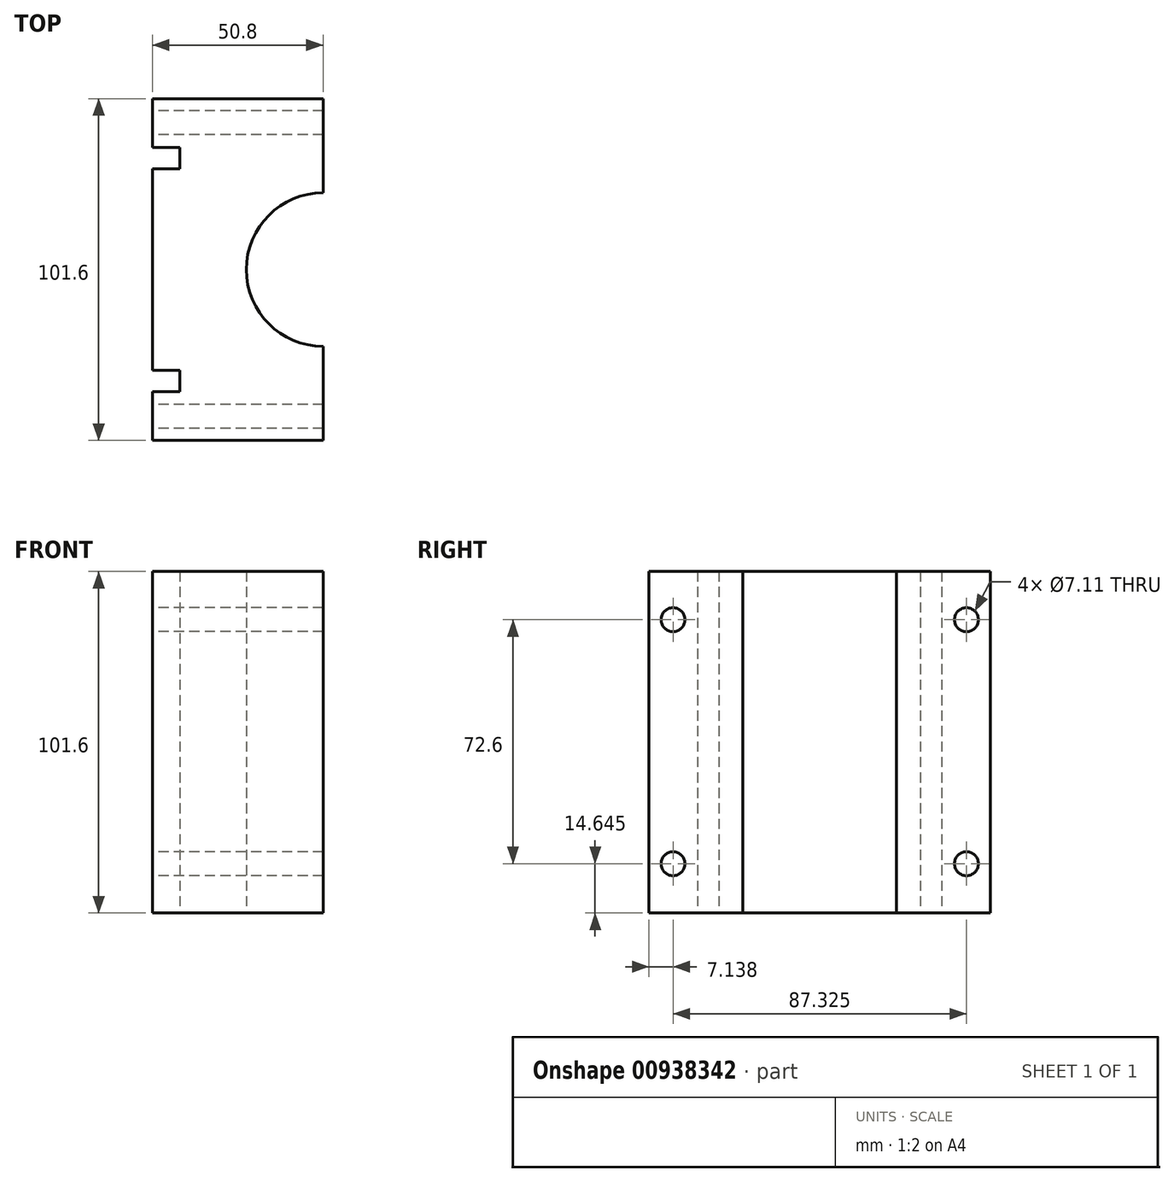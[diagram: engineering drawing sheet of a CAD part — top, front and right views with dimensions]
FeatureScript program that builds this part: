
annotation { "Feature Type Name" : "Feature", "Feature Type Description" : "" }
export const myFeature = defineFeature(function(context is Context, id is Id, definition is map)
    precondition{}
    {
        {
            var Q0;
            Q0=qCreatedBy(makeId("Top.planeOp"),FACE);
            var sketch = newSketch(context, id + "F0", { "sketchPlane" : qUnion([Q0])});
            skLineSegment(sketch, "E0.bottom", {"start": v(0, 0) * mm, "end": v(-50.8, 0) * mm});
            skLineSegment(sketch, "E0.top", {"start": v(0, 50.8) * mm, "end": v(-50.8, 50.8) * mm});
            skLineSegment(sketch, "E0.left", {"start": v(0, 0) * mm, "end": v(0, 50.8) * mm});
            skLineSegment(sketch, "E0.right", {"start": v(-50.8, 0) * mm, "end": v(-50.8, 50.8) * mm});
            skLineSegment(sketch, "E1.MirrorCS", {"start": v(0, 0) * mm, "end": v(0, -50.8) * mm});
            skLineSegment(sketch, "E2.MirrorCS", {"start": v(0, -50.8) * mm, "end": v(-50.8, -50.8) * mm});
            skLineSegment(sketch, "E3.MirrorCS", {"start": v(-50.8, 0) * mm, "end": v(-50.8, -50.8) * mm});
            skLineSegment(sketch, "E4", {"start": v(-50.8, 50.8) * mm, "end": v(-50.8, 36.32) * mm});
            skLineSegment(sketch, "E5", {"start": v(-50.8, 36.32) * mm, "end": v(-50.8, 29.97) * mm});
            skLineSegment(sketch, "E6", {"start": v(-50.8, 29.97) * mm, "end": v(-42.6, 29.97) * mm});
            skLineSegment(sketch, "E7", {"start": v(-42.6, 29.97) * mm, "end": v(-42.6, 36.32) * mm});
            skLineSegment(sketch, "E8", {"start": v(-42.6, 36.32) * mm, "end": v(-50.8, 36.32) * mm});
            skLineSegment(sketch, "E9.MirrorCS", {"start": v(-42.6, -36.32) * mm, "end": v(-50.8, -36.32) * mm});
            skLineSegment(sketch, "E10.MirrorCS", {"start": v(-50.8, -29.97) * mm, "end": v(-42.6, -29.97) * mm});
            skLineSegment(sketch, "E11.MirrorCS", {"start": v(-42.6, -29.97) * mm, "end": v(-42.6, -36.32) * mm});
            skCircle(sketch, "E12", {"center": v(0, 0) * mm, "radius": 22.86 * mm});
            skSolve(sketch);
        }
        {
            var Q0;
            {var subQ2=sQuery(id+"F0.wireOp",EDGE,"E0.top");Q0=makeQuery(id+"F0.imprint","IMPRINT",FACE,{"disambiguationData":[TD([[makeQuery(id+"F0.imprint","IMPRINT",EDGE,{"derivedFrom":subQ2}),1.0]])]});}
            var Q1;
            {var subQ4=sQuery(id+"F0.wireOp",EDGE,"E2.MirrorCS");Q1=makeQuery(id+"F0.imprint","IMPRINT",FACE,{"disambiguationData":[TD([[makeQuery(id+"F0.imprint","IMPRINT",EDGE,{"derivedFrom":subQ4}),-1.0]])]});}
            extrude(context, id + "F1", {"entities" : qUnion([Q0, Q1]), "depth" : 50.8 * mm, "offsetDistance" : 25.4 * mm});
        }
        {
            var Q0;
            Q0=makeQuery(id+"F1.opExtrude","CAP_FACE",FACE,{"disambiguationData":[OSD([sQuery(id+"F0.wireOp",EDGE,"E0.top"),sQuery(id+"F0.wireOp",EDGE,"E0.left"),sQuery(id+"F0.wireOp",EDGE,"E0.right"),sQuery(id+"F0.wireOp",EDGE,"E1.MirrorCS"),sQuery(id+"F0.wireOp",EDGE,"E2.MirrorCS"),sQuery(id+"F0.wireOp",EDGE,"E3.MirrorCS"),sQuery(id+"F0.wireOp",EDGE,"E4"),sQuery(id+"F0.wireOp",EDGE,"E6"),sQuery(id+"F0.wireOp",EDGE,"E7"),sQuery(id+"F0.wireOp",EDGE,"E8"),sQuery(id+"F0.wireOp",EDGE,"E9.MirrorCS"),sQuery(id+"F0.wireOp",EDGE,"E10.MirrorCS"),sQuery(id+"F0.wireOp",EDGE,"E11.MirrorCS"),sQuery(id+"F0.wireOp",EDGE,"E12")])],"isStart":false});
            extrude(context, id + "F2", {"entities" : qUnion([Q0]), "operationType" : NewBodyOperationType.ADD, "depth" : 50.8 * mm, "offsetDistance" : 25.4 * mm});
        }
        {
            var Q0;
            {var subQ0=sQuery(id+"F0.wireOp",EDGE,"E3.MirrorCS");Q0=makeQuery(id+"F2.boolean.opBoolean","MERGE",FACE,{"derivedFrom":[makeQuery(id+"F1.opExtrude","SWEPT_FACE",FACE,{"disambiguationData":[OSD([subQ0])]}),makeQuery(id+"F2.opExtrude","SWEPT_FACE",FACE,{"disambiguationData":[OSD([subQ0])]})]});}
            var sketch = newSketch(context, id + "F3", { "sketchPlane" : qUnion([Q0])});
            skCircle(sketch, "E13", {"center": v(43.66, 87.24) * mm, "radius": 5.08 * mm});
            skCircle(sketch, "E14.MirrorC", {"center": v(-43.66, 87.24) * mm, "radius": 5.08 * mm});
            skCircle(sketch, "E15", {"center": v(43.66, 14.65) * mm, "radius": 5.08 * mm});
            skCircle(sketch, "E16.MirrorC", {"center": v(-43.66, 14.65) * mm, "radius": 5.08 * mm});
            skCircle(sketch, "E17", {"center": v(-43.66, 87.24) * mm, "radius": 3.56 * mm});
            skCircle(sketch, "E18", {"center": v(43.66, 87.24) * mm, "radius": 3.56 * mm});
            skCircle(sketch, "E19", {"center": v(-43.66, 14.65) * mm, "radius": 3.56 * mm});
            skCircle(sketch, "E20", {"center": v(43.66, 14.65) * mm, "radius": 3.56 * mm});
            skSolve(sketch);
        }
        {
            var Q0;
            Q0=sQuery(id+"F3.wireOp",VERTEX,"E14.MirrorC.center");
            var Q1;
            Q1=sQuery(id+"F3.wireOp",VERTEX,"E13.center");
            var Q2;
            Q2=sQuery(id+"F3.wireOp",VERTEX,"E15.center");
            var Q3;
            Q3=sQuery(id+"F3.wireOp",VERTEX,"E16.MirrorC.center");
            var Q4;
            Q4=makeQuery(id+"F1.opExtrude","SWEPT_BODY",BODY,{"disambiguationData":[OSD([sQuery(id+"F0.wireOp",EDGE,"E0.top"),sQuery(id+"F0.wireOp",EDGE,"E0.left"),sQuery(id+"F0.wireOp",EDGE,"E0.right"),sQuery(id+"F0.wireOp",EDGE,"E1.MirrorCS"),sQuery(id+"F0.wireOp",EDGE,"E2.MirrorCS"),sQuery(id+"F0.wireOp",EDGE,"E3.MirrorCS"),sQuery(id+"F0.wireOp",EDGE,"E4"),sQuery(id+"F0.wireOp",EDGE,"E6"),sQuery(id+"F0.wireOp",EDGE,"E7"),sQuery(id+"F0.wireOp",EDGE,"E8"),sQuery(id+"F0.wireOp",EDGE,"E9.MirrorCS"),sQuery(id+"F0.wireOp",EDGE,"E10.MirrorCS"),sQuery(id+"F0.wireOp",EDGE,"E11.MirrorCS"),sQuery(id+"F0.wireOp",EDGE,"E12")])]});
            hole(context, id + "F4", {"style" : HoleStyle.SIMPLE, "endStyle" : HoleEndStyle.THROUGH, "holeDiameter" : 7.11 * mm, "majorDiameter" : 6.35 * mm, "isTappedThrough" : true, "tappedDepth" : 12.7 * mm, "tapClearance" : 3, "locations" : qUnion([Q0, Q1, Q2, Q3]), "scope" : qUnion([Q4])});
        }
    });
